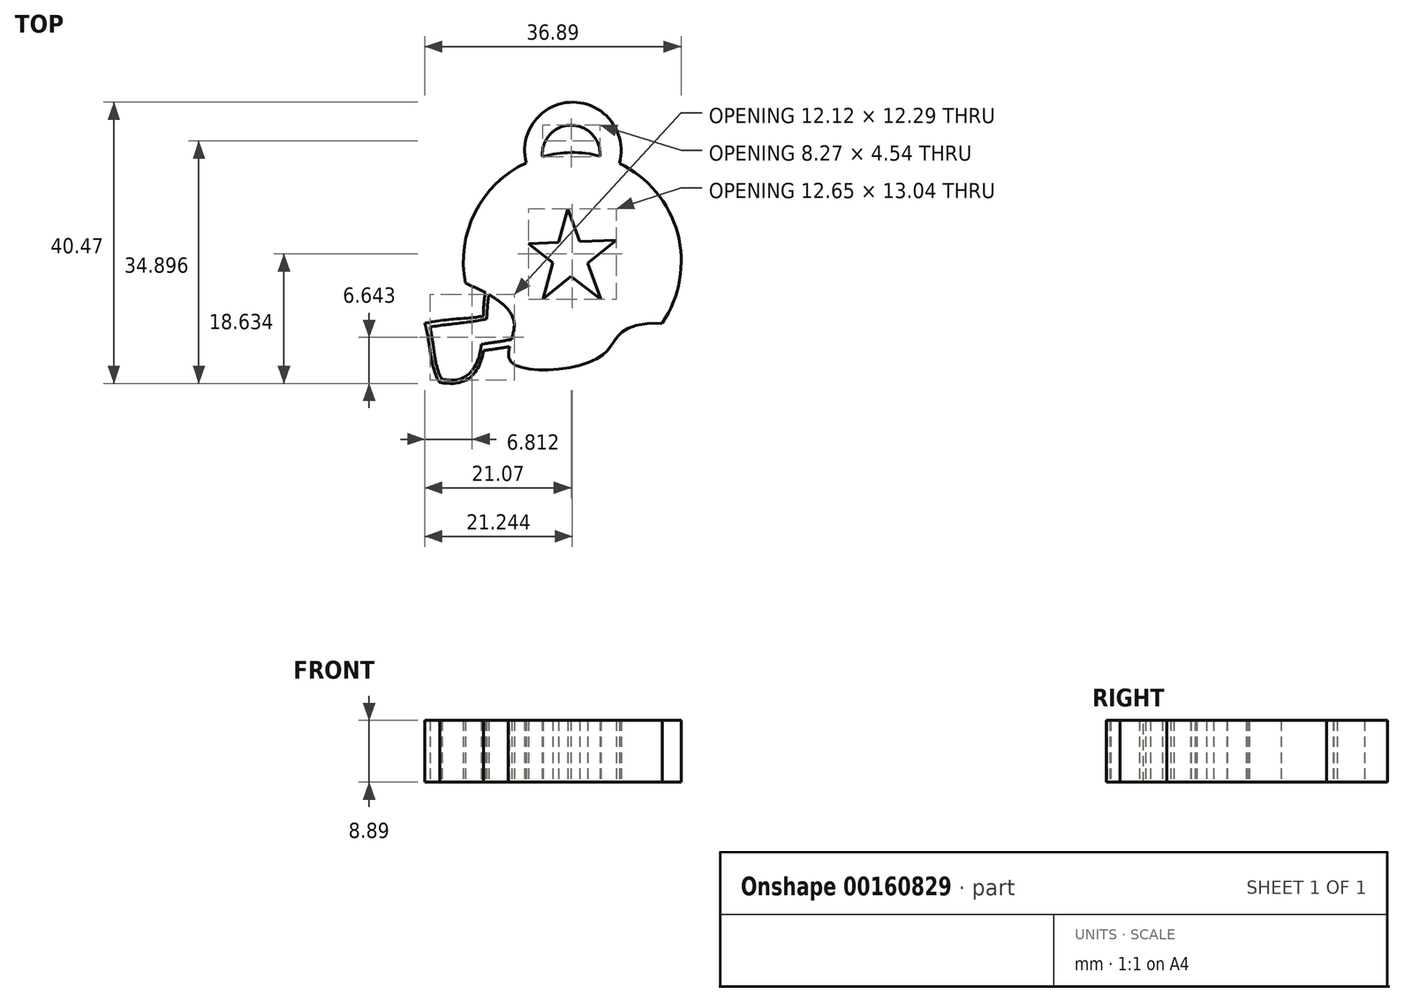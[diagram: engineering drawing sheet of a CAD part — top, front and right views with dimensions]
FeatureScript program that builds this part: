
annotation { "Feature Type Name" : "Feature", "Feature Type Description" : "" }
export const myFeature = defineFeature(function(context is Context, id is Id, definition is map)
    precondition{}
    {
        {
            var Q0;
            Q0=qCreatedBy(makeId("Top.planeOp"),FACE);
            var sketch = newSketch(context, id + "F0", { "sketchPlane" : qUnion([Q0])});
            skLineSegment(sketch, "E0", {"start": v(-27.04, 27.65) * mm, "end": v(-25.31, 22.9) * mm});
            skLineSegment(sketch, "E1", {"start": v(-22.3, 14.61) * mm, "end": v(-26.57, 17.9) * mm});
            skLineSegment(sketch, "E2", {"start": v(-32.7, 22.62) * mm, "end": v(-28.38, 22.79) * mm});
            skLineSegment(sketch, "E3", {"start": v(-20.05, 23.1) * mm, "end": v(-24.19, 19.8) * mm});
            skLineSegment(sketch, "E4", {"start": v(-30.62, 14.68) * mm, "end": v(-29.17, 19.9) * mm});
            skArc(sketch, "E5", {"start": v(-13.46, 11.2) * mm, "mid": v(-11.26, 24.11) * mm, "end": v(-19.63, 34.19) * mm});
            skFitSpline(sketch, "E6", {"points": [v(-41.75, 16.93) * mm, v(-34.76, 11.2) * mm, v(-35.22, 5.64) * mm, v(-22.3, 6.37) * mm, v(-13.46, 11.2) * mm], "startDerivative": vector(41.08, -17.95) * mm, "endDerivative": vector(86.18, 0) * mm});
            skFitSpline(sketch, "E7", {"points": [v(-38.36, 15.45) * mm, v(-45.47, 2.66) * mm], "startDerivative": vector(-2.69, -12.74) * mm, "endDerivative": vector(-24.3, 4.68) * mm});
            skFitSpline(sketch, "E8", {"points": [v(-45.47, 2.66) * mm, v(-47.62, 11.15) * mm], "startDerivative": vector(-4.1, 5.3) * mm, "endDerivative": vector(-2.29, 6.7) * mm});
            skFitSpline(sketch, "E9", {"points": [v(-47.62, 11.15) * mm, v(-36.2, 13.73) * mm], "startDerivative": vector(17.42, 3.7) * mm, "endDerivative": vector(9.17, 7.57) * mm});
            skFitSpline(sketch, "E10", {"points": [v(-46.83, 7.11) * mm, v(-31.38, 9.89) * mm], "startDerivative": vector(17.08, 3.3) * mm, "endDerivative": vector(15.12, 5.4) * mm});
            skFitSpline(sketch, "E11.0", {"points": [v(-46.66, 6.24) * mm, v(-43.87, 6.78) * mm, v(-40, 7.15) * mm, v(-34.95, 7.9) * mm, v(-32.38, 8.59) * mm, v(-31.08, 9.05) * mm]});
            skFitSpline(sketch, "E12.0", {"points": [v(-45.03, 3) * mm, v(-45.16, 3.18) * mm, v(-45.42, 3.63) * mm, v(-45.86, 4.85) * mm, v(-46.24, 6.8) * mm, v(-46.53, 8.87) * mm, v(-46.81, 10.36) * mm, v(-46.99, 11.03) * mm, v(-47.1, 11.33) * mm]});
            skFitSpline(sketch, "E13.trimOffspring", {"points": [v(-38.87, 15.56) * mm, v(-39, 15) * mm, v(-39.13, 13.7) * mm, v(-39.22, 11.49) * mm, v(-39.35, 9.16) * mm, v(-39.67, 6.94) * mm, v(-40.19, 5.36) * mm, v(-40.8, 4.37) * mm, v(-41.37, 3.78) * mm, v(-42.07, 3.34) * mm, v(-42.93, 3.07) * mm, v(-44, 2.98) * mm, v(-44.89, 3.08) * mm, v(-45.37, 3.17) * mm]});
            skFitSpline(sketch, "E14.trimOffspring", {"points": [v(-48.06, 10.3) * mm, v(-35.23, 13.17) * mm], "startDerivative": vector(10.82, 3.3) * mm, "endDerivative": vector(9.84, 6.73) * mm});
            skLineSegment(sketch, "E15.trimOffspring", {"start": v(-28.38, 22.79) * mm, "end": v(-27.04, 27.65) * mm});
            skLineSegment(sketch, "E16.trimOffspring", {"start": v(-24.19, 19.8) * mm, "end": v(-22.3, 14.61) * mm});
            skLineSegment(sketch, "E17.trimOffspring", {"start": v(-25.31, 22.9) * mm, "end": v(-20.05, 23.1) * mm});
            skLineSegment(sketch, "E18.trimOffspring", {"start": v(-26.57, 17.9) * mm, "end": v(-30.62, 14.68) * mm});
            skLineSegment(sketch, "E19.trimOffspring", {"start": v(-29.17, 19.9) * mm, "end": v(-32.7, 22.62) * mm});
            skFitSpline(sketch, "E20.0", {"points": [v(-37.87, 15.35) * mm, v(-37.97, 14.85) * mm, v(-38.1, 13.65) * mm, v(-38.2, 11.45) * mm, v(-38.33, 9.07) * mm, v(-38.66, 6.73) * mm, v(-39.23, 4.96) * mm, v(-39.98, 3.75) * mm, v(-40.71, 2.98) * mm, v(-41.64, 2.4) * mm, v(-43.12, 1.93) * mm, v(-44.5, 1.96) * mm, v(-45.56, 2.16) * mm]});
            skFitSpline(sketch, "E21.trimOffspring", {"points": [v(-45.03, 3) * mm, v(-45.16, 3.18) * mm, v(-45.42, 3.63) * mm, v(-45.86, 4.85) * mm, v(-46.24, 6.8) * mm, v(-46.53, 8.87) * mm, v(-46.81, 10.36) * mm, v(-46.99, 11.03) * mm, v(-47.1, 11.33) * mm]});
            skFitSpline(sketch, "E22.trimOffspring", {"points": [v(-46.66, 6.24) * mm, v(-43.87, 6.78) * mm, v(-40, 7.15) * mm, v(-34.95, 7.9) * mm, v(-32.38, 8.59) * mm, v(-31.08, 9.05) * mm]});
            skArc(sketch, "E23", {"start": v(-19.63, 34.19) * mm, "mid": v(-26.28, 42.97) * mm, "end": v(-33.03, 34.25) * mm});
            skArc(sketch, "E24.0", {"start": v(-22.42, 35.21) * mm, "mid": v(-26.6, 39.66) * mm, "end": v(-30.68, 35.13) * mm});
            skArc(sketch, "E25.trimOffspring", {"start": v(-22.42, 35.21) * mm, "mid": v(-26.56, 35.73) * mm, "end": v(-30.68, 35.13) * mm});
            skArc(sketch, "E26.trimOffspring", {"start": v(-33.03, 34.25) * mm, "mid": v(-40.4, 27.1) * mm, "end": v(-41.75, 16.93) * mm});
            skSolve(sketch);
        }
        {
            var Q0;
            Q0 = qSketchRegion(id + "F0", true);
            extrude(context, id + "F1", {"entities" : qUnion([Q0]), "domain" : OperationDomain.MODEL, "flatOperationType" : FlatOperationType.REMOVE, "depth" : 8.9 * mm, "offsetDistance" : 25.4 * mm});
        }
    });
